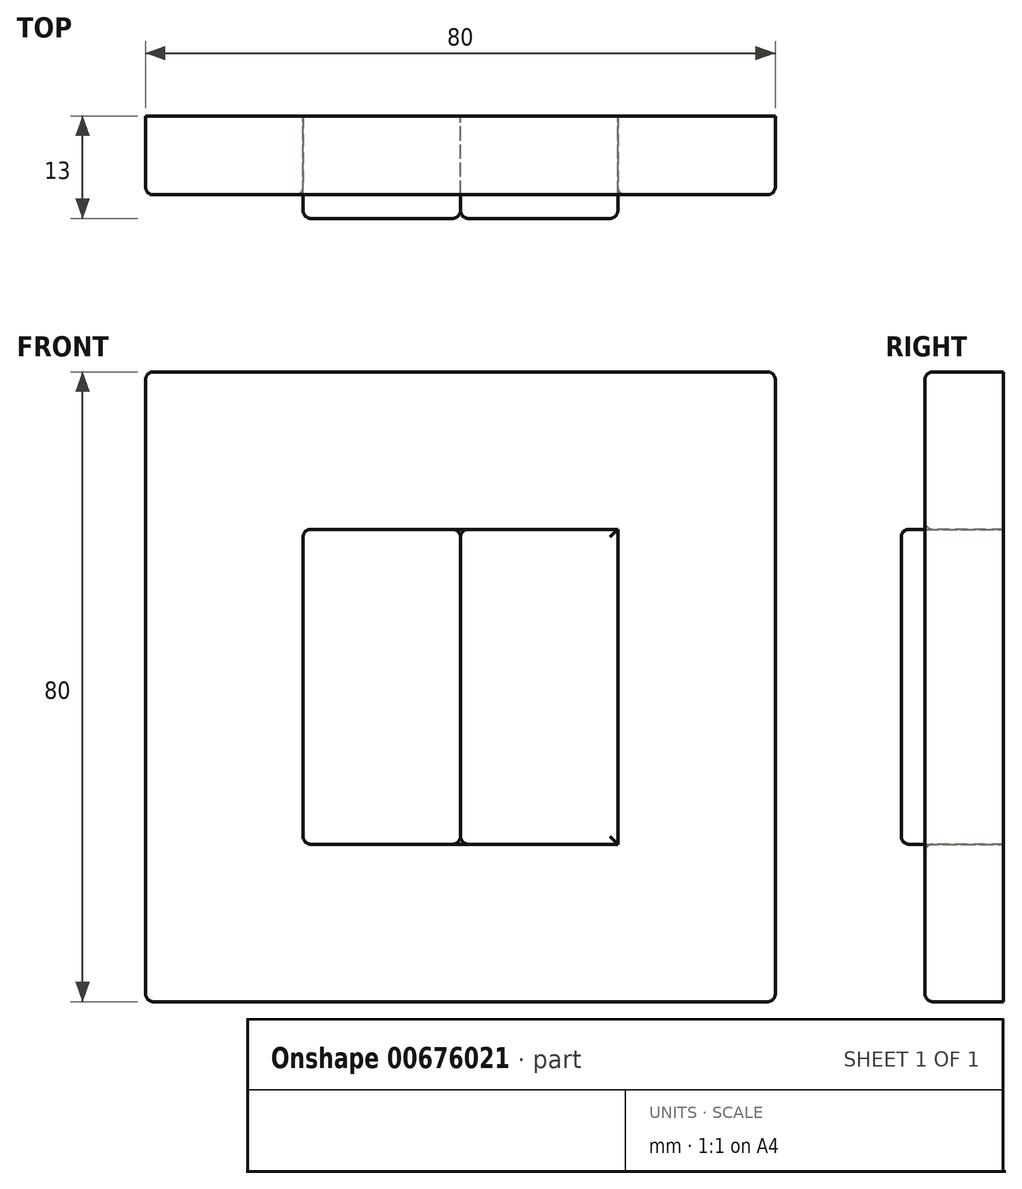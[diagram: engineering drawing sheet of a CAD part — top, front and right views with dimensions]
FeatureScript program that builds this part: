
annotation { "Feature Type Name" : "Feature", "Feature Type Description" : "" }
export const myFeature = defineFeature(function(context is Context, id is Id, definition is map)
    precondition{}
    {
        {
            var Q0;
            Q0=qCreatedBy(makeId("Front.planeOp"),FACE);
            var sketch = newSketch(context, id + "F0", { "sketchPlane" : qUnion([Q0])});
            skLineSegment(sketch, "E0.bottom", {"start": v(0, 0) * mm, "end": v(80, 0) * mm});
            skLineSegment(sketch, "E0.top", {"start": v(0, 80) * mm, "end": v(80, 80) * mm});
            skLineSegment(sketch, "E0.left", {"start": v(0, 0) * mm, "end": v(0, 80) * mm});
            skLineSegment(sketch, "E0.right", {"start": v(80, 0) * mm, "end": v(80, 80) * mm});
            skLineSegment(sketch, "E1.bottom", {"start": v(20, 60) * mm, "end": v(40, 60) * mm});
            skLineSegment(sketch, "E1.top", {"start": v(20, 20) * mm, "end": v(40, 20) * mm});
            skLineSegment(sketch, "E1.left", {"start": v(20, 60) * mm, "end": v(20, 20) * mm});
            skLineSegment(sketch, "E1.right", {"start": v(40, 60) * mm, "end": v(40, 20) * mm});
            skLineSegment(sketch, "E2.bottom", {"start": v(40, 60) * mm, "end": v(60, 60) * mm});
            skLineSegment(sketch, "E2.top", {"start": v(40, 20) * mm, "end": v(60, 20) * mm});
            skLineSegment(sketch, "E2.right", {"start": v(60, 60) * mm, "end": v(60, 20) * mm});
            skLineSegment(sketch, "E3", {"start": v(20, 40) * mm, "end": v(0, 40) * mm, "construction": true});
            skLineSegment(sketch, "E4", {"start": v(40, 60) * mm, "end": v(40, 80) * mm, "construction": true});
            skSolve(sketch);
        }
        {
            var Q0;
            Q0=makeQuery(id+"F0.imprint","IMPRINT",FACE,{"disambiguationData":[TD([[makeQuery(id+"F0.imprint","IMPRINT",EDGE,{"derivedFrom":sQuery(id+"F0.wireOp",EDGE,"E1.bottom")}),-1.0]])]});
            extrude(context, id + "F1", {"entities" : qUnion([Q0]), "depth" : 3 * mm, "offsetDistance" : 25 * mm, "hasSecondDirection" : true, "secondDirectionOppositeDirection" : true, "secondDirectionDepth" : 10 * mm});
        }
        {
            var Q0;
            Q0=makeQuery(id+"F0.imprint","IMPRINT",FACE,{"disambiguationData":[TD([[makeQuery(id+"F0.imprint","IMPRINT",EDGE,{"derivedFrom":sQuery(id+"F0.wireOp",EDGE,"huqwkKnN-88OR-snGu-hdvA-AZuDMS9QCH0S.bottom")}),-1.0]])]});
            var Q1;
            Q1=makeQuery(id+"F0.imprint","IMPRINT",FACE,{"disambiguationData":[TD([[makeQuery(id+"F0.imprint","IMPRINT",EDGE,{"derivedFrom":sQuery(id+"F0.wireOp",EDGE,"E2.bottom")}),-1.0]])]});
            extrude(context, id + "F2", {"entities" : qUnion([Q0, Q1]), "depth" : 3 * mm, "offsetDistance" : 25 * mm, "hasSecondDirection" : true, "secondDirectionOppositeDirection" : true, "secondDirectionDepth" : 10 * mm});
        }
        {
            var Q0;
            Q0=makeQuery(id+"F1.opExtrude","CAP_FACE",FACE,{"disambiguationData":[OSD([sQuery(id+"F0.wireOp",EDGE,"E1.bottom"),sQuery(id+"F0.wireOp",EDGE,"E1.top"),sQuery(id+"F0.wireOp",EDGE,"E1.left"),sQuery(id+"F0.wireOp",EDGE,"huqwkKnN-88OR-snGu-hdvA-AZuDMS9QCH0S.left")])],"isStart":false});
            var Q1;
            Q1=makeQuery(id+"F1.opExtrude","CAP_FACE",FACE,{"disambiguationData":[OSD([sQuery(id+"F0.wireOp",EDGE,"E2.bottom"),sQuery(id+"F0.wireOp",EDGE,"E2.top"),sQuery(id+"F0.wireOp",EDGE,"E1.right"),sQuery(id+"F0.wireOp",EDGE,"E2.right")])],"isStart":false});
            var Q2;
            Q2=makeQuery(id+"F1.opExtrude","SWEPT_EDGE",EDGE,{"disambiguationData":[OSD([sQuery(id+"F0.wireOp",EDGE,"huqwkKnN-88OR-snGu-hdvA-AZuDMS9QCH0S.bottom"),sQuery(id+"F0.wireOp",EDGE,"E2.bottom"),sQuery(id+"F0.wireOp",EDGE,"E1.right")])]});
            var Q3;
            Q3=makeQuery(id+"F1.opExtrude","SWEPT_EDGE",EDGE,{"disambiguationData":[OSD([sQuery(id+"F0.wireOp",EDGE,"E2.bottom"),sQuery(id+"F0.wireOp",EDGE,"E2.right")])]});
            var Q4;
            Q4=makeQuery(id+"F1.opExtrude","SWEPT_EDGE",EDGE,{"disambiguationData":[OSD([sQuery(id+"F0.wireOp",EDGE,"E1.bottom"),sQuery(id+"F0.wireOp",EDGE,"huqwkKnN-88OR-snGu-hdvA-AZuDMS9QCH0S.bottom"),sQuery(id+"F0.wireOp",EDGE,"huqwkKnN-88OR-snGu-hdvA-AZuDMS9QCH0S.left")])]});
            var Q5;
            Q5=makeQuery(id+"F1.opExtrude","SWEPT_EDGE",EDGE,{"disambiguationData":[OSD([sQuery(id+"F0.wireOp",EDGE,"E1.bottom"),sQuery(id+"F0.wireOp",EDGE,"E1.left")])]});
            var Q6;
            Q6=makeQuery(id+"F1.opExtrude","SWEPT_EDGE",EDGE,{"disambiguationData":[OSD([sQuery(id+"F0.wireOp",EDGE,"E1.top"),sQuery(id+"F0.wireOp",EDGE,"E1.left")])]});
            var Q7;
            Q7=makeQuery(id+"F1.opExtrude","SWEPT_EDGE",EDGE,{"disambiguationData":[OSD([sQuery(id+"F0.wireOp",EDGE,"E1.top"),sQuery(id+"F0.wireOp",EDGE,"huqwkKnN-88OR-snGu-hdvA-AZuDMS9QCH0S.top"),sQuery(id+"F0.wireOp",EDGE,"huqwkKnN-88OR-snGu-hdvA-AZuDMS9QCH0S.left")])]});
            var Q8;
            Q8=makeQuery(id+"F1.opExtrude","SWEPT_EDGE",EDGE,{"disambiguationData":[OSD([sQuery(id+"F0.wireOp",EDGE,"huqwkKnN-88OR-snGu-hdvA-AZuDMS9QCH0S.top"),sQuery(id+"F0.wireOp",EDGE,"E2.top"),sQuery(id+"F0.wireOp",EDGE,"E1.right")])]});
            var Q9;
            Q9=makeQuery(id+"F1.opExtrude","SWEPT_EDGE",EDGE,{"disambiguationData":[OSD([sQuery(id+"F0.wireOp",EDGE,"E2.top"),sQuery(id+"F0.wireOp",EDGE,"E2.right")])]});
            fillet(context, id + "F3", {"entities" : qUnion([Q0, Q1, Q2, Q3, Q4, Q5, Q6, Q7, Q8, Q9]), "radius" : 1 * mm, "tangentPropagation" : true, "allowEdgeOverflow" : false});
        }
        {
            var Q0;
            Q0=makeQuery(id+"F0.imprint","IMPRINT",FACE,{"disambiguationData":[TD([[makeQuery(id+"F0.imprint","IMPRINT",EDGE,{"derivedFrom":sQuery(id+"F0.wireOp",EDGE,"E0.bottom")}),1.0]])]});
            extrude(context, id + "F4", {"entities" : qUnion([Q0]), "oppositeDirection" : true, "depth" : 10 * mm, "offsetDistance" : 25 * mm});
        }
        {
            var Q0;
            Q0=makeQuery(id+"F2.opExtrude","CAP_FACE",FACE,{"disambiguationData":[OSD([sQuery(id+"F0.wireOp",EDGE,"huqwkKnN-88OR-snGu-hdvA-AZuDMS9QCH0S.bottom"),sQuery(id+"F0.wireOp",EDGE,"huqwkKnN-88OR-snGu-hdvA-AZuDMS9QCH0S.top"),sQuery(id+"F0.wireOp",EDGE,"huqwkKnN-88OR-snGu-hdvA-AZuDMS9QCH0S.left"),sQuery(id+"F0.wireOp",EDGE,"E1.right")])],"isStart":false});
            var Q1;
            Q1=makeQuery(id+"F2.opExtrude","SWEPT_EDGE",EDGE,{"disambiguationData":[OSD([sQuery(id+"F0.wireOp",EDGE,"E1.bottom"),sQuery(id+"F0.wireOp",EDGE,"huqwkKnN-88OR-snGu-hdvA-AZuDMS9QCH0S.bottom"),sQuery(id+"F0.wireOp",EDGE,"huqwkKnN-88OR-snGu-hdvA-AZuDMS9QCH0S.left")])]});
            var Q2;
            Q2=makeQuery(id+"F2.opExtrude","SWEPT_EDGE",EDGE,{"disambiguationData":[OSD([sQuery(id+"F0.wireOp",EDGE,"huqwkKnN-88OR-snGu-hdvA-AZuDMS9QCH0S.bottom"),sQuery(id+"F0.wireOp",EDGE,"E2.bottom"),sQuery(id+"F0.wireOp",EDGE,"E1.right")])]});
            var Q3;
            Q3=makeQuery(id+"F2.opExtrude","SWEPT_EDGE",EDGE,{"disambiguationData":[OSD([sQuery(id+"F0.wireOp",EDGE,"huqwkKnN-88OR-snGu-hdvA-AZuDMS9QCH0S.top"),sQuery(id+"F0.wireOp",EDGE,"E2.top"),sQuery(id+"F0.wireOp",EDGE,"E1.right")])]});
            var Q4;
            Q4=makeQuery(id+"F2.opExtrude","SWEPT_EDGE",EDGE,{"disambiguationData":[OSD([sQuery(id+"F0.wireOp",EDGE,"E1.top"),sQuery(id+"F0.wireOp",EDGE,"huqwkKnN-88OR-snGu-hdvA-AZuDMS9QCH0S.top"),sQuery(id+"F0.wireOp",EDGE,"huqwkKnN-88OR-snGu-hdvA-AZuDMS9QCH0S.left")])]});
            var Q5;
            Q5=makeQuery(id+"F4.opExtrude","CAP_EDGE",EDGE,{"disambiguationData":[OSD([sQuery(id+"F0.wireOp",EDGE,"E0.top")])],"isStart":true});
            var Q6;
            Q6=makeQuery(id+"F4.opExtrude","SWEPT_EDGE",EDGE,{"disambiguationData":[OSD([sQuery(id+"F0.wireOp",EDGE,"E0.top"),sQuery(id+"F0.wireOp",EDGE,"E0.left")])]});
            var Q7;
            Q7=makeQuery(id+"F4.opExtrude","CAP_EDGE",EDGE,{"disambiguationData":[OSD([sQuery(id+"F0.wireOp",EDGE,"E0.left")])],"isStart":true});
            var Q8;
            Q8=makeQuery(id+"F4.opExtrude","CAP_EDGE",EDGE,{"disambiguationData":[OSD([sQuery(id+"F0.wireOp",EDGE,"E0.bottom")])],"isStart":true});
            var Q9;
            Q9=makeQuery(id+"F4.opExtrude","SWEPT_EDGE",EDGE,{"disambiguationData":[OSD([sQuery(id+"F0.wireOp",EDGE,"E0.bottom"),sQuery(id+"F0.wireOp",EDGE,"E0.left")])]});
            var Q10;
            Q10=makeQuery(id+"F4.opExtrude","SWEPT_EDGE",EDGE,{"disambiguationData":[OSD([sQuery(id+"F0.wireOp",EDGE,"E0.top"),sQuery(id+"F0.wireOp",EDGE,"E0.right")])]});
            var Q11;
            Q11=makeQuery(id+"F4.opExtrude","CAP_EDGE",EDGE,{"disambiguationData":[OSD([sQuery(id+"F0.wireOp",EDGE,"E0.right")])],"isStart":true});
            var Q12;
            Q12=makeQuery(id+"F4.opExtrude","SWEPT_EDGE",EDGE,{"disambiguationData":[OSD([sQuery(id+"F0.wireOp",EDGE,"E0.bottom"),sQuery(id+"F0.wireOp",EDGE,"E0.right")])]});
            var Q13;
            Q13=makeQuery(id+"F4.opExtrude","CAP_EDGE",EDGE,{"disambiguationData":[OSD([sQuery(id+"F0.wireOp",EDGE,"E1.bottom"),sQuery(id+"F0.wireOp",EDGE,"huqwkKnN-88OR-snGu-hdvA-AZuDMS9QCH0S.bottom"),sQuery(id+"F0.wireOp",EDGE,"E2.bottom")])],"isStart":true});
            var Q14;
            Q14=makeQuery(id+"F4.opExtrude","CAP_EDGE",EDGE,{"disambiguationData":[OSD([sQuery(id+"F0.wireOp",EDGE,"E1.left")])],"isStart":true});
            var Q15;
            Q15=makeQuery(id+"F4.opExtrude","CAP_EDGE",EDGE,{"disambiguationData":[OSD([sQuery(id+"F0.wireOp",EDGE,"E2.right")])],"isStart":true});
            var Q16;
            Q16=makeQuery(id+"F4.opExtrude","CAP_EDGE",EDGE,{"disambiguationData":[OSD([sQuery(id+"F0.wireOp",EDGE,"E1.top"),sQuery(id+"F0.wireOp",EDGE,"huqwkKnN-88OR-snGu-hdvA-AZuDMS9QCH0S.top"),sQuery(id+"F0.wireOp",EDGE,"E2.top")])],"isStart":true});
            var Q17;
            Q17=makeQuery(id+"F4.opExtrude","SWEPT_EDGE",EDGE,{"disambiguationData":[OSD([sQuery(id+"F0.wireOp",EDGE,"E2.top"),sQuery(id+"F0.wireOp",EDGE,"E2.right")])]});
            var Q18;
            Q18=makeQuery(id+"F4.opExtrude","SWEPT_EDGE",EDGE,{"disambiguationData":[OSD([sQuery(id+"F0.wireOp",EDGE,"E2.bottom"),sQuery(id+"F0.wireOp",EDGE,"E2.right")])]});
            var Q19;
            Q19=makeQuery(id+"F4.opExtrude","SWEPT_EDGE",EDGE,{"disambiguationData":[OSD([sQuery(id+"F0.wireOp",EDGE,"E1.bottom"),sQuery(id+"F0.wireOp",EDGE,"E1.left")])]});
            var Q20;
            Q20=makeQuery(id+"F4.opExtrude","SWEPT_EDGE",EDGE,{"disambiguationData":[OSD([sQuery(id+"F0.wireOp",EDGE,"E1.top"),sQuery(id+"F0.wireOp",EDGE,"E1.left")])]});
            fillet(context, id + "F5", {"entities" : qUnion([Q0, Q1, Q2, Q3, Q4, Q5, Q6, Q7, Q8, Q9, Q10, Q11, Q12, Q13, Q14, Q15, Q16, Q17, Q18, Q19, Q20]), "radius" : 1 * mm, "tangentPropagation" : true, "allowEdgeOverflow" : false});
        }
    });
